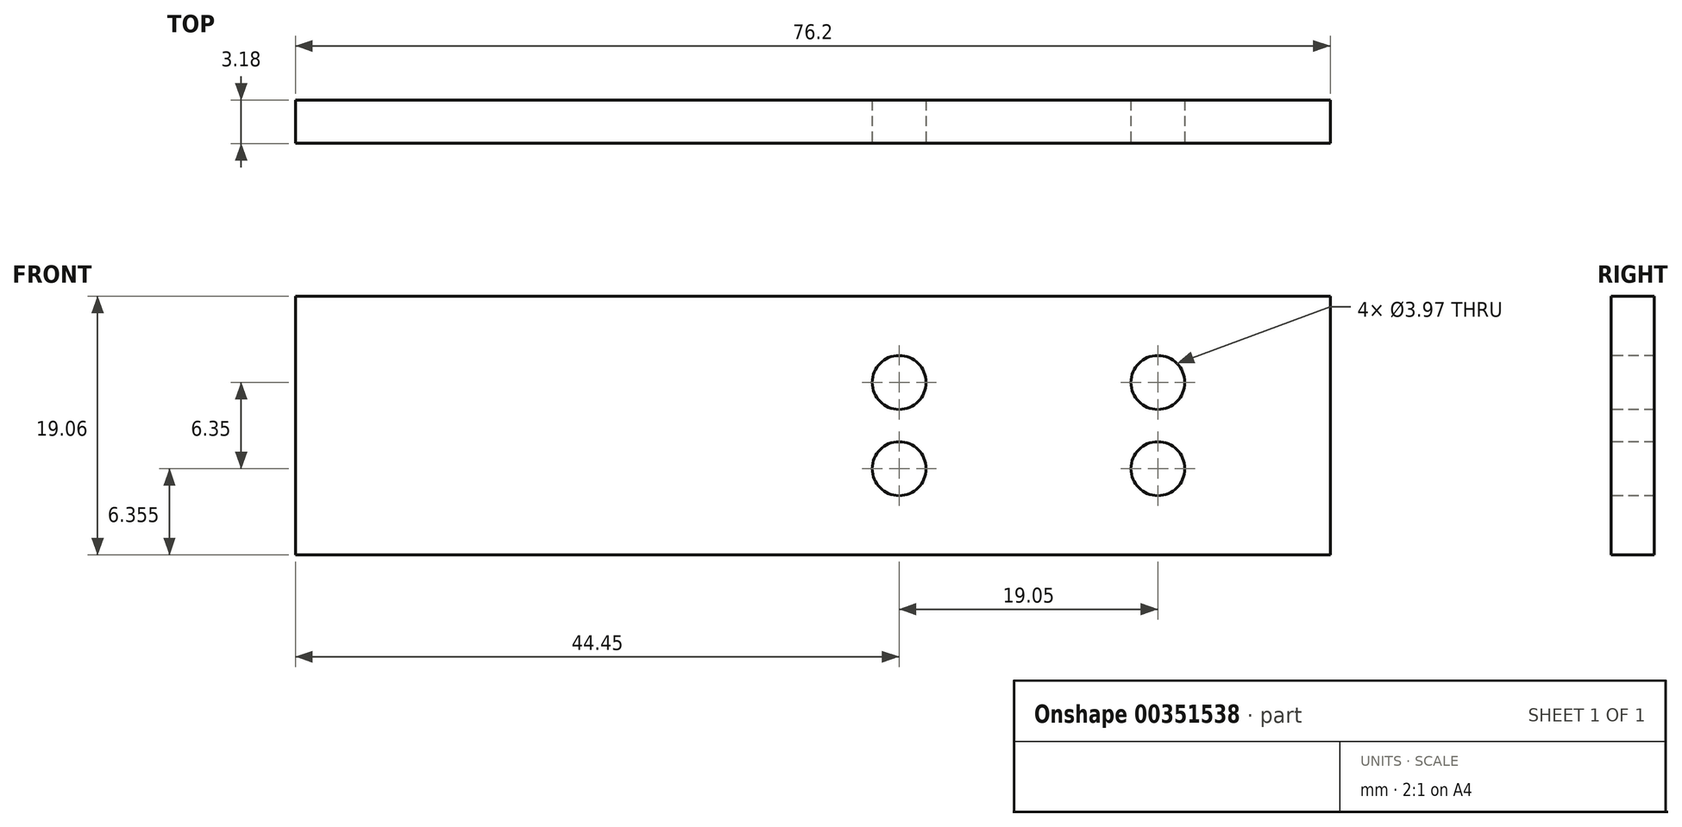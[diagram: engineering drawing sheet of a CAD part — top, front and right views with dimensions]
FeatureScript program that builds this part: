
annotation { "Feature Type Name" : "Feature", "Feature Type Description" : "" }
export const myFeature = defineFeature(function(context is Context, id is Id, definition is map)
    precondition{}
    {
        {
            var Q0;
            Q0=qCreatedBy(makeId("Front.planeOp"),FACE);
            var sketch = newSketch(context, id + "F0", { "sketchPlane" : qUnion([Q0])});
            skLineSegment(sketch, "E0.bottom", {"start": v(38.1, 9.53) * mm, "end": v(-38.1, 9.53) * mm});
            skLineSegment(sketch, "E0.top", {"start": v(38.1, -9.53) * mm, "end": v(-38.1, -9.53) * mm});
            skLineSegment(sketch, "E0.left", {"start": v(38.1, 9.53) * mm, "end": v(38.1, -9.53) * mm});
            skLineSegment(sketch, "E0.right", {"start": v(-38.1, 9.53) * mm, "end": v(-38.1, -9.53) * mm});
            skPoint(sketch, "E0.middle", {"position": v(0, 0) * mm});
            skSolve(sketch);
        }
        {
            var Q0;
            Q0 = qSketchRegion(id + "F0", true);
            extrude(context, id + "F1", {"entities" : qUnion([Q0]), "depth" : 3.17 * mm, "symmetric" : true});
        }
        {
            var Q0;
            Q0=makeQuery(id+"F1.opExtrude","CAP_FACE",FACE,{"disambiguationData":[OSD([sQuery(id+"F0.wireOp",EDGE,"E0.bottom"),sQuery(id+"F0.wireOp",EDGE,"E0.top"),sQuery(id+"F0.wireOp",EDGE,"E0.left"),sQuery(id+"F0.wireOp",EDGE,"E0.right")])],"isStart":false});
            var sketch = newSketch(context, id + "F2", { "sketchPlane" : qUnion([Q0])});
            skCircle(sketch, "E1", {"center": v(25.4, 3.18) * mm, "radius": 1.98 * mm});
            skCircle(sketch, "E2", {"center": v(25.4, -3.18) * mm, "radius": 1.98 * mm});
            skCircle(sketch, "E3", {"center": v(6.35, 3.17) * mm, "radius": 1.98 * mm});
            skCircle(sketch, "E4", {"center": v(6.35, -3.18) * mm, "radius": 1.98 * mm});
            skSolve(sketch);
        }
        {
            var Q0;
            Q0 = qSketchRegion(id + "F2", true);
            extrude(context, id + "F3", {"entities" : qUnion([Q0]), "operationType" : NewBodyOperationType.REMOVE, "endBound" : BoundingType.THROUGH_ALL, "oppositeDirection" : true, "depth" : 25.4 * mm});
        }
    });
